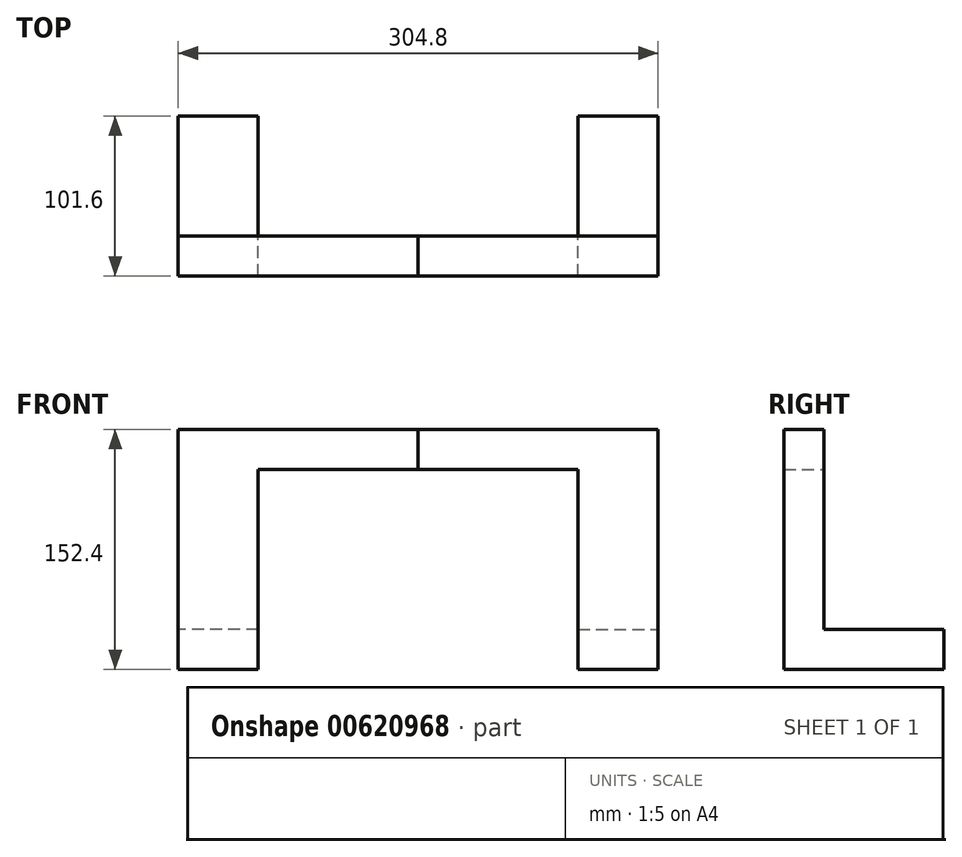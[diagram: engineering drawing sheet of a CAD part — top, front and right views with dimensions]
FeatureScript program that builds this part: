
annotation { "Feature Type Name" : "Feature", "Feature Type Description" : "" }
export const myFeature = defineFeature(function(context is Context, id is Id, definition is map)
    precondition{}
    {
        {
            var Q0;
            Q0=qCreatedBy(makeId("Top.planeOp"),FACE);
            var sketch = newSketch(context, id + "F0", { "sketchPlane" : qUnion([Q0])});
            skLineSegment(sketch, "E0.bottom", {"start": v(12.7, -12.7) * mm, "end": v(-12.7, -12.7) * mm});
            skLineSegment(sketch, "E0.top", {"start": v(12.7, 12.7) * mm, "end": v(-12.7, 12.7) * mm});
            skLineSegment(sketch, "E0.left", {"start": v(12.7, -12.7) * mm, "end": v(12.7, 12.7) * mm});
            skLineSegment(sketch, "E0.right", {"start": v(-12.7, -12.7) * mm, "end": v(-12.7, 12.7) * mm});
            skPoint(sketch, "E0.middle", {"position": v(0, 0) * mm});
            skSolve(sketch);
        }
        {
            var Q0;
            Q0=makeQuery(id+"F0.imprint","IMPRINT",FACE,{"disambiguationData":[TD([[makeQuery(id+"F0.imprint","IMPRINT",EDGE,{"derivedFrom":sQuery(id+"F0.wireOp",EDGE,"E0.bottom")}),-1.0]])]});
            extrude(context, id + "F1", {"entities" : qUnion([Q0]), "depth" : 127 * mm, "offsetDistance" : 25.4 * mm});
        }
        {
            var Q0;
            Q0=makeQuery(id+"F1.opExtrude","CAP_FACE",FACE,{"disambiguationData":[OSD([sQuery(id+"F0.wireOp",EDGE,"E0.bottom"),sQuery(id+"F0.wireOp",EDGE,"E0.top"),sQuery(id+"F0.wireOp",EDGE,"E0.left"),sQuery(id+"F0.wireOp",EDGE,"E0.right")])],"isStart":false});
            var sketch = newSketch(context, id + "F2", { "sketchPlane" : qUnion([Q0])});
            skLineSegment(sketch, "E1.bottom", {"start": v(-12.7, 12.7) * mm, "end": v(114.3, 12.7) * mm});
            skLineSegment(sketch, "E1.top", {"start": v(-12.7, -12.7) * mm, "end": v(114.3, -12.7) * mm});
            skLineSegment(sketch, "E1.left", {"start": v(-12.7, 12.7) * mm, "end": v(-12.7, -12.7) * mm});
            skLineSegment(sketch, "E1.right", {"start": v(114.3, 12.7) * mm, "end": v(114.3, -12.7) * mm});
            skSolve(sketch);
        }
        {
            var Q0;
            Q0 = qSketchRegion(id + "F2", true);
            extrude(context, id + "F3", {"entities" : qUnion([Q0]), "operationType" : NewBodyOperationType.ADD, "depth" : 25.4 * mm, "offsetDistance" : 25.4 * mm});
        }
        {
            var Q0;
            Q0=makeQuery(id+"F1.opExtrude","CAP_FACE",FACE,{"disambiguationData":[OSD([sQuery(id+"F0.wireOp",EDGE,"E0.bottom"),sQuery(id+"F0.wireOp",EDGE,"E0.top"),sQuery(id+"F0.wireOp",EDGE,"E0.left"),sQuery(id+"F0.wireOp",EDGE,"E0.right")])],"isStart":true});
            var sketch = newSketch(context, id + "F4", { "sketchPlane" : qUnion([Q0])});
            skLineSegment(sketch, "E2.bottom", {"start": v(12.7, 12.7) * mm, "end": v(-38.1, 12.7) * mm});
            skLineSegment(sketch, "E2.top", {"start": v(12.7, -88.9) * mm, "end": v(-38.1, -88.9) * mm});
            skLineSegment(sketch, "E2.left", {"start": v(12.7, 12.7) * mm, "end": v(12.7, -88.9) * mm});
            skLineSegment(sketch, "E2.right", {"start": v(-38.1, 12.7) * mm, "end": v(-38.1, -88.9) * mm});
            skSolve(sketch);
        }
        {
            var Q0;
            {var subQ3=sQuery(id+"F4.wireOp",EDGE,"E2.top");Q0=makeQuery(id+"F4.imprint","IMPRINT",FACE,{"disambiguationData":[TD([[makeQuery(id+"F4.imprint","IMPRINT",EDGE,{"derivedFrom":subQ3}),-1.0]])]});}
            extrude(context, id + "F5", {"entities" : qUnion([Q0]), "operationType" : NewBodyOperationType.ADD, "oppositeDirection" : true, "depth" : 25.4 * mm, "offsetDistance" : 25.4 * mm});
        }
        {
            var Q0;
            Q0=makeQuery(id+"F5.opExtrude","CAP_FACE",FACE,{"disambiguationData":[OSD([sQuery(id+"F0.wireOp",EDGE,"E0.top"),sQuery(id+"F0.wireOp",EDGE,"E0.right"),sQuery(id+"F4.wireOp",EDGE,"E2.bottom"),sQuery(id+"F4.wireOp",EDGE,"E2.top"),sQuery(id+"F4.wireOp",EDGE,"E2.left"),sQuery(id+"F4.wireOp",EDGE,"E2.right")])],"isStart":false});
            var sketch = newSketch(context, id + "F6", { "sketchPlane" : qUnion([Q0])});
            skLineSegment(sketch, "E3.bottom", {"start": v(-38.1, -12.7) * mm, "end": v(-12.7, -12.7) * mm});
            skLineSegment(sketch, "E3.top", {"start": v(-38.1, 12.7) * mm, "end": v(-12.7, 12.7) * mm});
            skLineSegment(sketch, "E3.left", {"start": v(-38.1, -12.7) * mm, "end": v(-38.1, 12.7) * mm});
            skLineSegment(sketch, "E3.right", {"start": v(-12.7, -12.7) * mm, "end": v(-12.7, 12.7) * mm});
            skSolve(sketch);
        }
        {
            var Q0;
            Q0 = qSketchRegion(id + "F6", true);
            extrude(context, id + "F7", {"entities" : qUnion([Q0]), "operationType" : NewBodyOperationType.ADD, "depth" : 127 * mm, "offsetDistance" : 25.4 * mm});
        }
        {
            var Q0;
            Q0=makeQuery(id+"F1.opExtrude","SWEPT_BODY",BODY,{"disambiguationData":[OSD([sQuery(id+"F0.wireOp",EDGE,"E0.bottom"),sQuery(id+"F0.wireOp",EDGE,"E0.top"),sQuery(id+"F0.wireOp",EDGE,"E0.left"),sQuery(id+"F0.wireOp",EDGE,"E0.right")])]});
            var Q1;
            Q1=makeQuery(id+"F3.opExtrude","SWEPT_FACE",FACE,{"disambiguationData":[OSD([sQuery(id+"F2.wireOp",EDGE,"E1.right")])]});
            mirror(context, id + "F8", {"entities" : qUnion([Q0]), "mirrorPlane" : qUnion([Q1])});
        }
    });
